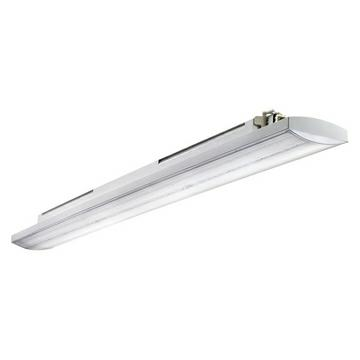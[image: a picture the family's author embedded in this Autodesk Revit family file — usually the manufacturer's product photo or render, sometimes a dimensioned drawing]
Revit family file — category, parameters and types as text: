
# Revit family: Lighting-Industrial-GEWISS-SMART[3]PLUS-WATERTIGHT-LED_TRANSPARENT_MEDBEAM_1600mm
name_source: partatom
category: Apparecchi per illuminazione
units: mm (PartAtom-declared; Revit-internal decimal feet)

## family parameters
Condiviso = No
Host = Superficie
Punto di calcolo locali = No
Quota connettore circolare = Usa diametro
Sorgente d'illuminazione = Sì
Taglio con vuoti quando caricato = No
Tipo di parte = Normale

## types (1)
- Lighting-Industrial-GEWISS-SMART[3]PLUS-WATERTIGHT-LED_TRANSPARENT_MEDBEAM_1600mm
    Angolo inclinazione = -90.00°
    Application = Indoor
    Carico apparente = 67 VA
    Catalogue = LIGHTING
    Catalogue Range = SMART[3] PLUS
    Colour temperature = 5700 K (CRI > 90)
    Colour temperature: = 5700 K (CRI > 90)
    Commenti sul wattaggio = 67W
    Descrizione = SMART3 PLUS 1600 T.W.DALI HE CONC 9 57
    Efficiency class of integrated LEDs = A ÷ A++
    Electrocod = 2434
    Emetti da lunghezza linea = 1200 mm
    File diagramma fotometrico = GWS3323AC957.IES
    Filtro dei colori = 16777215
    Ganci = Alluminio
    Glow Wire Test = 850°C
    IDF = c62d0f5f-3b46-4599-86a8-f38eb5caca3c
    IDT = fe96ae85-68db-4e0d-8c9b-145f0d7eb605
    IP degree = IP66/IP69
    Immagine tipo = GWS3280TS.jpg
    Insulation class = II
    Lamp = LED
    Lampada = LED
    Length = 1600 mm
    Lumen output (lm) = 5600
    Lunghezza Lampada = 1600 mm  [stored 5.24934 ft]
    Modello = GWS3323AC957
    Numero poli = 2
    Operating temperature: = -25 +50 °C
    Produttore = GEWISS S.p.A.
    Prospetto di default = 1219 mm
    SEO = Ceiling
    Schermo. = Led Acceso
    Shield type = Transparent
    Shock resistance = IK08
    Stampa 1_100 = Sì
    Stampa 1_200 = No
    Struttura = GRIGIO
    System power = 50 W
    Technical sheet = https://www.gewiss.com
    Type of light source = LED - Not replaceable
    Typology = DALI
    URL = https://www.gewiss.com
    Variazione temperatura colore lampada con luminosità attenuata = <Nessuno>
    Version file RFA = 20.0
    Voltage = 220-240 V
    Warranty = 5 years
    Working temperature = -25 +50 °C

note: [stored X ft] marks values corroborated as IEEE doubles in the binary element streams (Revit-internal decimal feet)
